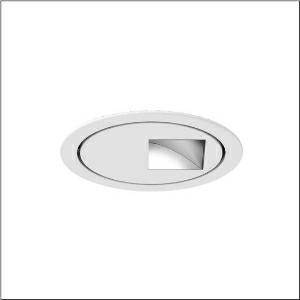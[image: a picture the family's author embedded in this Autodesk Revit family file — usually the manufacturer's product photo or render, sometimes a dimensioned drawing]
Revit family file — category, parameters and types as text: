
# Revit family: lunis_11_mini_round_51dk11b72wf21
name_source: partatom
category: Lighting Fixtures
units: mm (PartAtom-declared; Revit-internal decimal feet)

## family parameters
Cut with Voids When Loaded = No
Host = Face
Light Source = No
Part Type = Normal
Room Calculation Point = No
Round Connector Dimension = Use Diameter
Shared = No

## types (1)
- Lunis 11 mini round (1 x LED 3000K / CRI = 80 (unbekannt), 2380 lm, 3000K)
    Apparent Load = 28 VA
    CIE Flux Codes = 44 77 97 100 100
    Color Rendering = 80
    Color Temperature = 3000K
    Default Elevation = 1800 mm
    Description = Lunis 11 mini round, downlight, light control with wallwasher, of highly reflective aluminium, highly specular, light emission: direct distribution, LED rated luminous flux: 2.380lm, light colour: 830, control gear: ECG, with terminal, 3-pole, mains connection: 220..230V, AC/DC, 0/50..60Hz, LED module, luminaire module, of aluminium, highly specular, white, diameter: 176mm, clamping range: 1..40mm, recessing ring, of plastic, traffic white (RAL 9016), protection rating (complete): IP20, insulation class (complete): insulation class II (safety insulation), certification: CE, permissible ambient temperature for indoor applications: 0..+35°C, packaging unit: 1 piece
    Height = 0 mm  [stored 0 ft]
    Lamp = 1 x LED 3000K / CRI >= 80 (unbekannt)
    Lamp Light Flux = 2380 lm
    Lamp count = 1
    Length = 176 mm
    Luminous efficacy = 85 lm/W
    Manufacturer = Siteco
    ModVariant = No
    Model = 51DK11B72WF21
    Mounting Place = Ceiling
    Mounting Type = Recessed
    Number of Poles = 1
    OnlyDefault = Yes
    Power Factor = 1
    Product Name = Lunis 11 mini round
    Product group = downlight | ceiling recessed
    ProductGroupID = 402
    Protection Class = Protection class II
    Protection Degree = IP 20
    RLX_Detail_Level = 1
    RlxData = <blob elided: 59329 chars, md5=ce6ce3ef>
    Socket = socket
    Standby Power = 0 W
    System Light Flux = 2380 lm
    System Power = 28 W
    Type Comments = Product without accessories
    Type Image = l_1004772.jpg
    URL = http://relux.com
    VarID = ---
    Voltage = 0 V
    Weight = 0.00 kg
    Width = 176 mm

note: [stored X ft] marks values corroborated as IEEE doubles in the binary element streams (Revit-internal decimal feet)

## geometry (parser evidence)
native form markers: Blend x4, Sweep x10
no freeform markers — native parametric forms only
